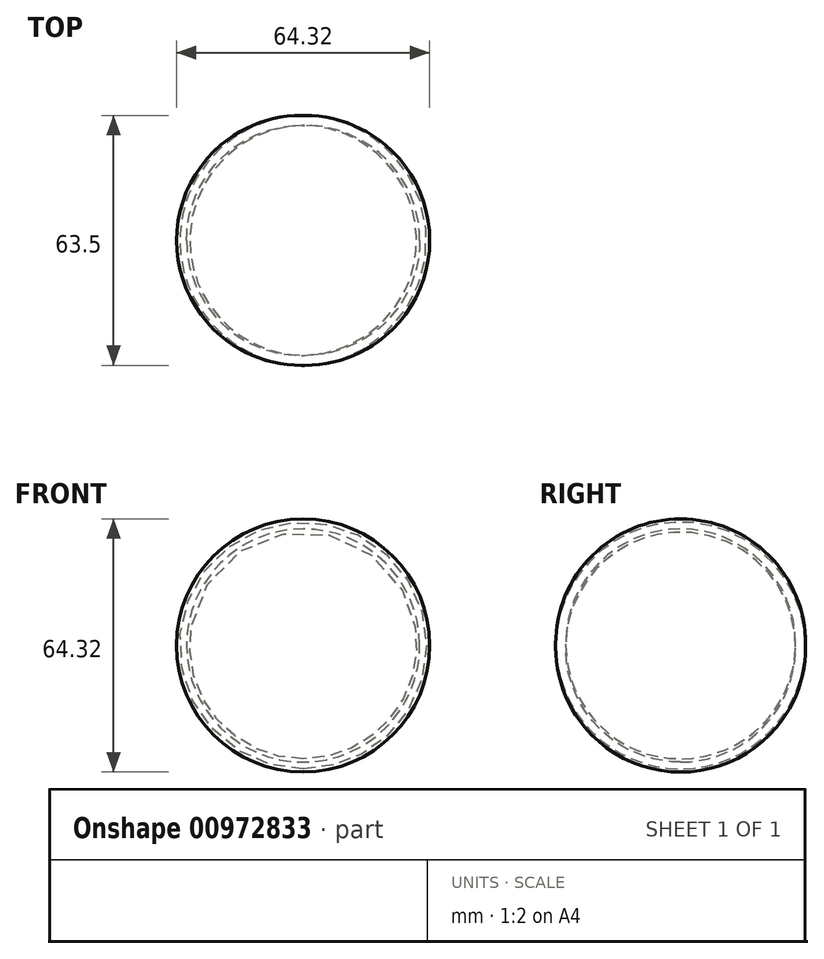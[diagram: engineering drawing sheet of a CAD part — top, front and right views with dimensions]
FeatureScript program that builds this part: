
annotation { "Feature Type Name" : "Feature", "Feature Type Description" : "" }
export const myFeature = defineFeature(function(context is Context, id is Id, definition is map)
    precondition{}
    {
        {
            var Q0;
            Q0=qCreatedBy(makeId("Top.planeOp"),FACE);
            var sketch = newSketch(context, id + "F0", { "sketchPlane" : qUnion([Q0])});
            skLineSegment(sketch, "E0", {"start": v(0, 0) * mm, "end": v(0, -31.75) * mm});
            skLineSegment(sketch, "E1", {"start": v(0, 0) * mm, "end": v(0, 31.75) * mm});
            skArc(sketch, "E2", {"start": v(0, -31.75) * mm, "mid": v(32.16, 0) * mm, "end": v(0, 31.75) * mm});
            skSolve(sketch);
        }
        {
            var Q0;
            Q0=qCreatedBy(makeId("Front.planeOp"),FACE);
            var sketch = newSketch(context, id + "F1", { "sketchPlane" : qUnion([Q0])});
            skPoint(sketch, "E3", {"position": v(31.75, 0) * mm});
            skCircle(sketch, "E4", {"center": v(0, 0) * mm, "radius": 31.75 * mm});
            skSolve(sketch);
        }
        {
            var Q0;
            Q0=makeQuery(id+"F0.imprint","IMPRINT",FACE,{"disambiguationData":[TD([[makeQuery(id+"F0.imprint","IMPRINT",EDGE,{"derivedFrom":sQuery(id+"F0.wireOp",EDGE,"E0")}),1.0]])]});
            var Q1;
            Q1=sQuery(id+"F1.wireOp",EDGE,"E4");
            revolve(context, id + "F2", {"surfaceOperationType" : NewSurfaceOperationType.NEW, "entities" : qUnion([Q0]), "axis" : qUnion([Q1]), "revolveType" : RevolveType.FULL});
        }
        {
            var Q0;
            Q0=makeQuery(id+"F2.opRevolve","SWEPT_FACE",FACE,{"disambiguationData":[OSD([sQuery(id+"F0.wireOp",EDGE,"E2")])]});
            var Q1;
            Q1=makeQuery(id+"F2.opRevolve","SWEPT_BODY",BODY,{"disambiguationData":[OSD([sQuery(id+"F0.wireOp",EDGE,"E0"),sQuery(id+"F0.wireOp",EDGE,"E1"),sQuery(id+"F0.wireOp",EDGE,"E2")])]});
            shell(context, id + "F3", {"isHollow" : true, "entities" : qUnion([Q0]), "parts" : qUnion([Q1]), "thickness" : 2.54 * mm});
        }
    });
